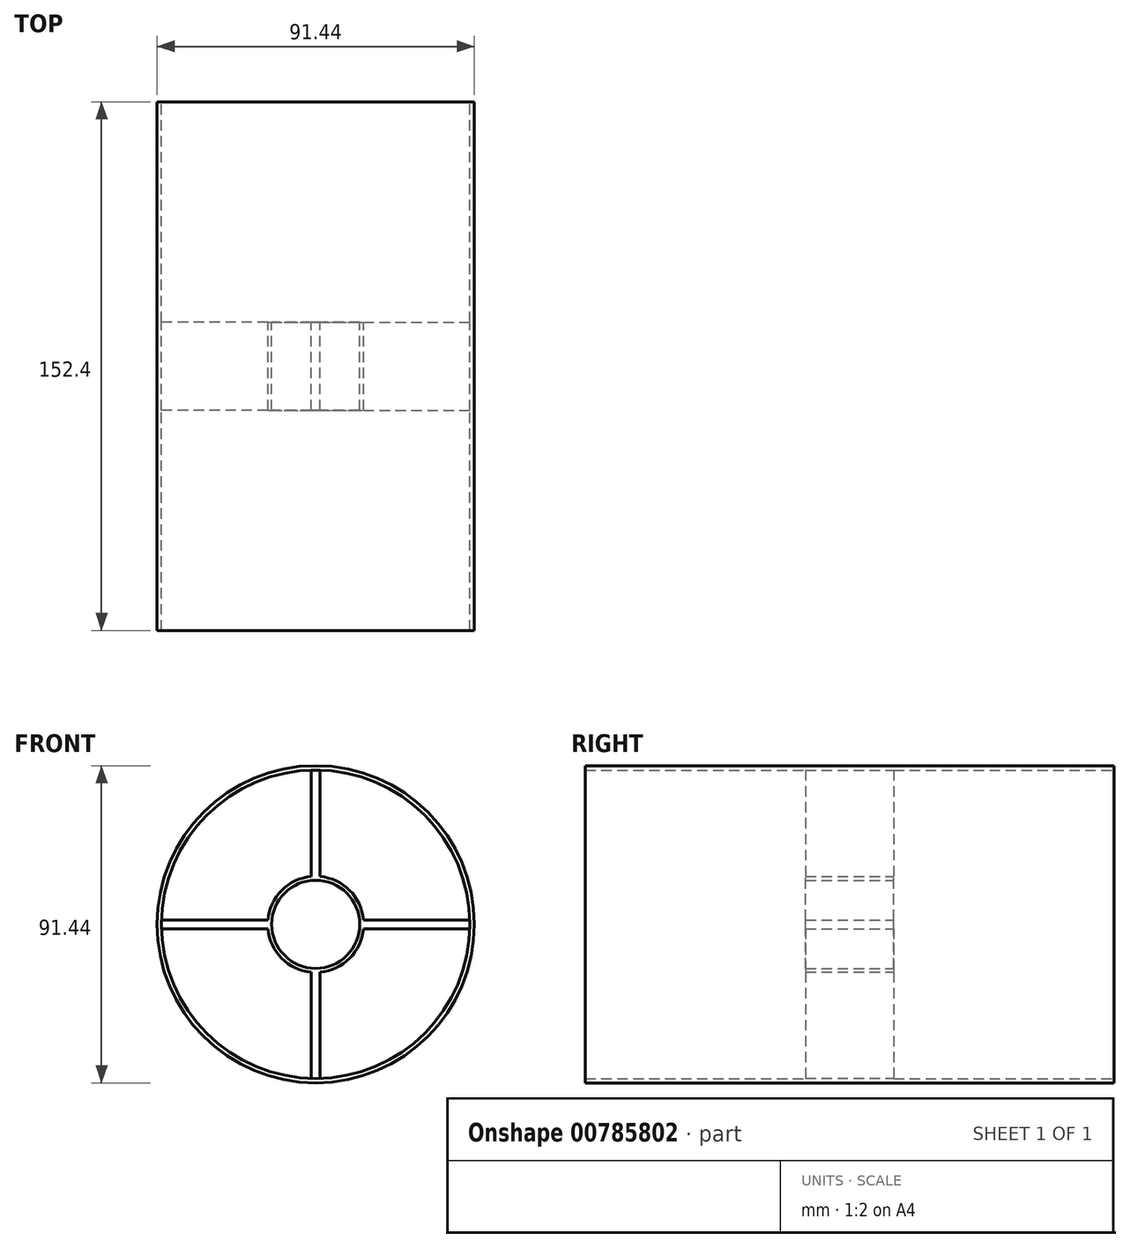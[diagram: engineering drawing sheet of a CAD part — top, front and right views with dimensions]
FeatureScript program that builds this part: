
annotation { "Feature Type Name" : "Feature", "Feature Type Description" : "" }
export const myFeature = defineFeature(function(context is Context, id is Id, definition is map)
    precondition{}
    {
        {
            var Q0;
            Q0=qCreatedBy(makeId("Front.planeOp"),FACE);
            var sketch = newSketch(context, id + "F0", { "sketchPlane" : qUnion([Q0])});
            skCircle(sketch, "E0", {"center": v(0, 0) * mm, "radius": 44.45 * mm});
            skCircle(sketch, "E1", {"center": v(0, 0) * mm, "radius": 12.7 * mm});
            skLineSegment(sketch, "E2", {"start": v(0, 12.7) * mm, "end": v(0, 44.45) * mm});
            skLineSegment(sketch, "E3", {"start": v(12.7, 0) * mm, "end": v(44.45, 0) * mm});
            skLineSegment(sketch, "E4", {"start": v(-12.7, 0) * mm, "end": v(-44.45, 0) * mm});
            skLineSegment(sketch, "E5", {"start": v(0, -12.7) * mm, "end": v(0, -44.45) * mm});
            skLineSegment(sketch, "E6", {"start": v(1.27, 44.43) * mm, "end": v(1.27, 12.64) * mm});
            skLineSegment(sketch, "E7", {"start": v(-44.43, 1.27) * mm, "end": v(-12.64, 1.27) * mm});
            skLineSegment(sketch, "E8", {"start": v(44.43, 1.27) * mm, "end": v(12.64, 1.27) * mm});
            skLineSegment(sketch, "E9", {"start": v(-1.27, -12.64) * mm, "end": v(-1.27, -44.43) * mm});
            skLineSegment(sketch, "E10", {"start": v(-12.64, -1.27) * mm, "end": v(-44.43, -1.27) * mm});
            skLineSegment(sketch, "E11", {"start": v(12.64, -1.27) * mm, "end": v(44.43, -1.27) * mm});
            skLineSegment(sketch, "E12", {"start": v(1.27, -12.64) * mm, "end": v(1.27, -44.43) * mm});
            skCircle(sketch, "E13", {"center": v(0, 0) * mm, "radius": 45.72 * mm});
            skLineSegment(sketch, "E14", {"start": v(-1.27, 44.43) * mm, "end": v(-1.27, 12.64) * mm});
            skCircle(sketch, "E15", {"center": v(0, 0) * mm, "radius": 13.84 * mm});
            skSolve(sketch);
        }
        {
            var Q0;
            Q0=makeQuery(id+"F0.imprint","IMPRINT",FACE,{"disambiguationData":[TD([[makeQuery(id+"F0.imprint","IMPRINT",EDGE,{"derivedFrom":sQuery(id+"F0.wireOp",EDGE,"E13")}),1.0]])]});
            extrude(context, id + "F1", {"entities" : qUnion([Q0]), "endBound" : BoundingType.SYMMETRIC, "depth" : 152.4 * mm, "offsetDistance" : 25.4 * mm});
        }
        {
            var Q0;
            {var subQ0=sQuery(id+"F0.wireOp",EDGE,"E4");Q0=makeQuery(id+"F0.imprint","IMPRINT",FACE,{"disambiguationData":[TD([[makeQuery(id+"F0.imprint","IMPRINT",EDGE,{"derivedFrom":subQ0}),-1.0]])]});}
            var Q1;
            {var subQ0=sQuery(id+"F0.wireOp",EDGE,"E2");Q1=makeQuery(id+"F0.imprint","IMPRINT",FACE,{"disambiguationData":[TD([[makeQuery(id+"F0.imprint","IMPRINT",EDGE,{"derivedFrom":subQ0}),-1.0]])]});}
            var Q2;
            {var subQ0=sQuery(id+"F0.wireOp",EDGE,"E3");Q2=makeQuery(id+"F0.imprint","IMPRINT",FACE,{"disambiguationData":[TD([[makeQuery(id+"F0.imprint","IMPRINT",EDGE,{"derivedFrom":subQ0}),1.0]])]});}
            var Q3;
            {var subQ0=sQuery(id+"F0.wireOp",EDGE,"E5");Q3=makeQuery(id+"F0.imprint","IMPRINT",FACE,{"disambiguationData":[TD([[makeQuery(id+"F0.imprint","IMPRINT",EDGE,{"derivedFrom":subQ0}),-1.0]])]});}
            var Q4;
            {var subQ0=sQuery(id+"F0.wireOp",EDGE,"E5");Q4=makeQuery(id+"F0.imprint","IMPRINT",FACE,{"disambiguationData":[TD([[makeQuery(id+"F0.imprint","IMPRINT",EDGE,{"derivedFrom":subQ0}),1.0]])]});}
            var Q5;
            {var subQ0=sQuery(id+"F0.wireOp",EDGE,"E4");Q5=makeQuery(id+"F0.imprint","IMPRINT",FACE,{"disambiguationData":[TD([[makeQuery(id+"F0.imprint","IMPRINT",EDGE,{"derivedFrom":subQ0}),1.0]])]});}
            var Q6;
            {var subQ0=sQuery(id+"F0.wireOp",EDGE,"E3");Q6=makeQuery(id+"F0.imprint","IMPRINT",FACE,{"disambiguationData":[TD([[makeQuery(id+"F0.imprint","IMPRINT",EDGE,{"derivedFrom":subQ0}),-1.0]])]});}
            var Q7;
            {var subQ0=sQuery(id+"F0.wireOp",EDGE,"E9");var subQ1=sQuery(id+"F0.wireOp",EDGE,"E1");var subQ2=makeQuery(id+"F0.imprint","INTERSECT",VERTEX,{"derivedFrom":[subQ1,subQ0]});Q7=makeQuery(id+"F0.imprint","IMPRINT",FACE,{"disambiguationData":[TD([[makeQuery(id+"F0.imprint","IMPRINT",EDGE,{"disambiguationData":[TD([[subQ2,1.0]])],"derivedFrom":subQ1}),-1.0]])]});}
            var Q8;
            {var subQ0=sQuery(id+"F0.wireOp",EDGE,"E11");var subQ1=sQuery(id+"F0.wireOp",EDGE,"E1");var subQ2=makeQuery(id+"F0.imprint","INTERSECT",VERTEX,{"derivedFrom":[subQ1,subQ0]});Q8=makeQuery(id+"F0.imprint","IMPRINT",FACE,{"disambiguationData":[TD([[makeQuery(id+"F0.imprint","IMPRINT",EDGE,{"disambiguationData":[TD([[subQ2,1.0]])],"derivedFrom":subQ1}),-1.0]])]});}
            var Q9;
            {var subQ0=sQuery(id+"F0.wireOp",EDGE,"E6");var subQ1=sQuery(id+"F0.wireOp",EDGE,"E1");var subQ2=makeQuery(id+"F0.imprint","INTERSECT",VERTEX,{"derivedFrom":[subQ1,subQ0]});Q9=makeQuery(id+"F0.imprint","IMPRINT",FACE,{"disambiguationData":[TD([[makeQuery(id+"F0.imprint","IMPRINT",EDGE,{"disambiguationData":[TD([[subQ2,1.0]])],"derivedFrom":subQ1}),-1.0]])]});}
            var Q10;
            {var subQ0=sQuery(id+"F0.wireOp",EDGE,"E7");var subQ1=sQuery(id+"F0.wireOp",EDGE,"E1");var subQ2=makeQuery(id+"F0.imprint","INTERSECT",VERTEX,{"derivedFrom":[subQ1,subQ0]});Q10=makeQuery(id+"F0.imprint","IMPRINT",FACE,{"disambiguationData":[TD([[makeQuery(id+"F0.imprint","IMPRINT",EDGE,{"disambiguationData":[TD([[subQ2,1.0]])],"derivedFrom":subQ1}),-1.0]])]});}
            var Q11;
            {var subQ0=sQuery(id+"F0.wireOp",EDGE,"E2");var subQ1=sQuery(id+"F0.wireOp",EDGE,"E0");var subQ2=makeQuery(id+"F0.imprint","INTERSECT",VERTEX,{"derivedFrom":[subQ1,subQ0]});Q11=makeQuery(id+"F0.imprint","IMPRINT",FACE,{"disambiguationData":[TD([[makeQuery(id+"F0.imprint","IMPRINT",EDGE,{"disambiguationData":[TD([[subQ2,-1.0]])],"derivedFrom":subQ1}),1.0]])]});}
            var Q12;
            {var subQ0=sQuery(id+"F0.wireOp",EDGE,"E2");var subQ1=sQuery(id+"F0.wireOp",EDGE,"E1");var subQ2=makeQuery(id+"F0.imprint","INTERSECT",VERTEX,{"derivedFrom":[subQ1,subQ0]});Q12=makeQuery(id+"F0.imprint","IMPRINT",FACE,{"disambiguationData":[TD([[makeQuery(id+"F0.imprint","IMPRINT",EDGE,{"disambiguationData":[TD([[subQ2,-1.0]])],"derivedFrom":subQ1}),-1.0]])]});}
            extrude(context, id + "F2", {"entities" : qUnion([Q0, Q1, Q2, Q3, Q4, Q5, Q6, Q7, Q8, Q9, Q10, Q11, Q12]), "operationType" : NewBodyOperationType.ADD, "endBound" : BoundingType.SYMMETRIC, "depth" : 25.4 * mm, "offsetDistance" : 25.4 * mm});
        }
    });
